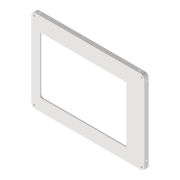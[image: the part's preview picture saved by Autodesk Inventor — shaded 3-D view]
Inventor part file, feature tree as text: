
AUTODESK INVENTOR PART (.ipt)
format: ipt  version: 2022 (Build 260153000, 153)  size: 241,152 bytes
history: native  units: mm
features: sketch x7, extrude x6, reference x6, other x4, projected_geometry x2, hole x1
ambient origin geometry x8: Origin, YZ Plane, XZ Plane, XY Plane, X Axis, Y Axis, Z Axis, Center Point
bodies: Volumenkörper1 (feature_tree)
feature tree (26):
  extrude  "Extrusion1"  Depth=2.0mm
  extrude  "Extrusion2"  Depth=5.0mm
  hole  "Bohrung1"  [1 undecoded]
  extrude  "Extrusion3"  Depth=2.8mm
  extrude  "Extrusion4"  Depth=2.8mm
  extrude  "Extrusion5"  Depth=4.0mm
  extrude  "Extrusion6"  Depth=20.0mm
  sketch  "Skizze1"  dims[d0=1.0mm d1=2.0mm]
  reference  "Referenz1"
  reference  "Referenz2"
  sketch  "Skizze2"  dims[d2=5.0mm d3=5.0mm]
  reference  "Referenz3"
  projected_geometry  "Projizierte Kontur1"
  sketch  "Skizze3"  dims[d5=0.0mm d6=1.0mm]
  projected_geometry  "Projizierte Kontur2"
  sketch  "Skizze4"  dims[d8=0.0mm d9=2.8mm]
  reference  "Referenz4"
  sketch  "Skizze5"  dims[d10=2.8mm d11=2.8mm]
  sketch  "Skizze6"  dims[d12=2.8mm d13=4.0mm]
  reference  "Referenz5"
  reference  "Referenz6"
  sketch  "Skizze7"  dims[d14=4.0mm d15=4.0mm d16=4.0mm d17=4.0mm d18=4.0mm d19=4.0mm d20=4.0mm d21=2.8mm d22=6.0mm d23=7.0mm d24=9.0mm d25=90.0deg d26=8.0mm d27=20.594885mm d28=2.8mm d29=3.0mm d30=2.8mm d31=20.0mm d32=0.0mm d33=20.0mm d34=0.0mm d35=2.8mm d36=3.0mm d37=2.8mm d38=20.0mm d39=0.0mm d40=20.0mm d41=0.0mm]
  other  "Omnicscope_Xiao.iam"
  other  "00_24wellplate_base:1"
  other  "Omniscope_USBC_Base_Top+:1"
  other  "Omniscope_USBC_Base:1"
note: 1 required parameter value undecoded (feature->parameter linkage not recoverable at this tier; creation-order binding heuristic only, values carry confidence <= 0.55)
